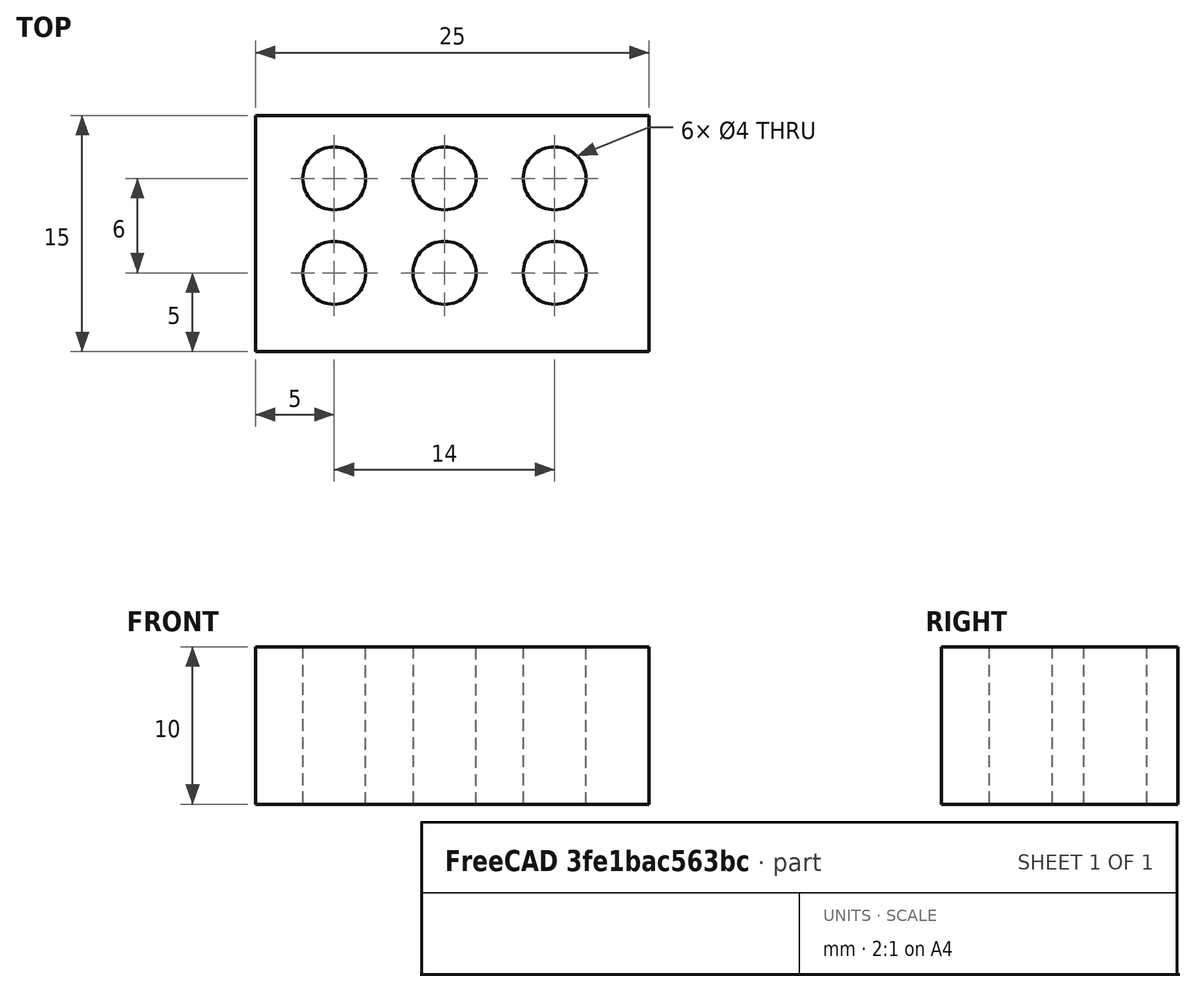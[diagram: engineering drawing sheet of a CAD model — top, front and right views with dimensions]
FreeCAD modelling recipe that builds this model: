
FCSTD DOCUMENT  (FreeCAD 0.20R29177 (Git))
Label: Ejercicio2Video9
License: All rights reserved
LicenseURL: http://en.wikipedia.org/wiki/All_rights_reserved
objects: Part::Cylinder×6, Part::MultiFuse×3, Part::Box×1, Part::Fuse×1, Part::Cut×1
note: 12 computed .brp shape members not serialized (recipe doc carries the construction recipe); baked Part::Feature solids carry a one-line shape summary decoded from their .brp

FEATURE [Part::Box] Box  label="Cubo"
  AttacherType = Attacher::AttachEngine3D
  Height = 10
  Length = 25
  Width = 15
FEATURE [Part::Cylinder] Cylinder  label="Cilindro"
  Angle = 360
  AttacherType = Attacher::AttachEngine3D
  FirstAngle = 0
  Height = 10
  Placement = pos=(5,5,0) rot=(0,0,1;0rad)
  Radius = 2
  SecondAngle = 0
FEATURE [Part::Cylinder] Cylinder001  label="Cilindro001"
  Angle = 360
  AttacherType = Attacher::AttachEngine3D
  FirstAngle = 0
  Height = 10
  Placement = pos=(12,5,0) rot=(0,0,1;0rad)
  Radius = 2
  SecondAngle = 0
FEATURE [Part::Cylinder] Cylinder002  label="Cilindro002"
  Angle = 360
  AttacherType = Attacher::AttachEngine3D
  FirstAngle = 0
  Height = 10
  Placement = pos=(19,5,0) rot=(0,0,1;0rad)
  Radius = 2
  SecondAngle = 0
FEATURE [Part::Cylinder] Cylinder003  label="Cilindro003"
  Angle = 360
  AttacherType = Attacher::AttachEngine3D
  FirstAngle = 0
  Height = 10
  Placement = pos=(5,11,0) rot=(0,0,1;0rad)
  Radius = 2
  SecondAngle = 0
FEATURE [Part::Cylinder] Cylinder004  label="Cilindro004"
  Angle = 360
  AttacherType = Attacher::AttachEngine3D
  FirstAngle = 0
  Height = 10
  Placement = pos=(12,11,0) rot=(0,0,1;0rad)
  Radius = 2
  SecondAngle = 0
FEATURE [Part::Cylinder] Cylinder005  label="Cilindro005"
  Angle = 360
  AttacherType = Attacher::AttachEngine3D
  FirstAngle = 0
  Height = 10
  Placement = pos=(19,11,0) rot=(0,0,1;0rad)
  Radius = 2
  SecondAngle = 0
FEATURE [Part::Fuse] Fusion
  Base = -> Cylinder004
  Tool = -> Cylinder005
FEATURE [Part::MultiFuse] Fusion001
  Shapes = -> [Cylinder003,Cylinder002]
FEATURE [Part::MultiFuse] Fusion002
  Shapes = -> [Cylinder001,Cylinder]
FEATURE [Part::MultiFuse] Fusion003  label="agujeros"
  Shapes = -> [Fusion002,Fusion,Fusion001]
FEATURE [Part::Cut] Cut  label="ladrillo"
  Base = -> Box
  Tool = -> Fusion003
